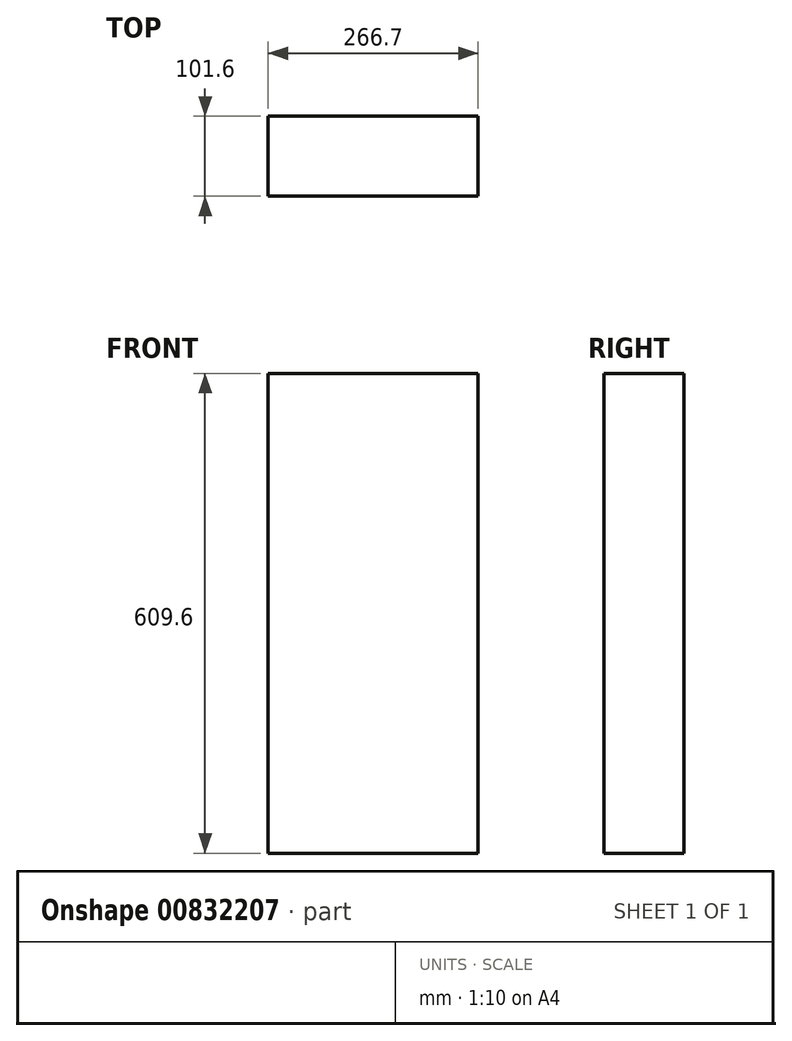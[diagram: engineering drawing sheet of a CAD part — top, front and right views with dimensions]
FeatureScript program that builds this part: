
annotation { "Feature Type Name" : "Feature", "Feature Type Description" : "" }
export const myFeature = defineFeature(function(context is Context, id is Id, definition is map)
    precondition{}
    {
        {
            var Q0;
            Q0=qCreatedBy(makeId("Front.planeOp"),FACE);
            var sketch = newSketch(context, id + "F0", { "sketchPlane" : qUnion([Q0])});
            skLineSegment(sketch, "E0.bottom", {"start": v(133.35, 304.8) * mm, "end": v(-133.35, 304.8) * mm});
            skLineSegment(sketch, "E0.top", {"start": v(133.35, -304.8) * mm, "end": v(-133.35, -304.8) * mm});
            skLineSegment(sketch, "E0.left", {"start": v(133.35, 304.8) * mm, "end": v(133.35, -304.8) * mm});
            skLineSegment(sketch, "E0.right", {"start": v(-133.35, 304.8) * mm, "end": v(-133.35, -304.8) * mm});
            skPoint(sketch, "E0.middle", {"position": v(0, 0) * mm});
            skSolve(sketch);
        }
        {
            var Q0;
            Q0=qSketchRegion(id+"F0",true);
            extrude(context, id + "F1", {"entities" : qUnion([Q0]), "depth" : 101.6 * mm, "offsetDistance" : 25.4 * mm});
        }
    });
